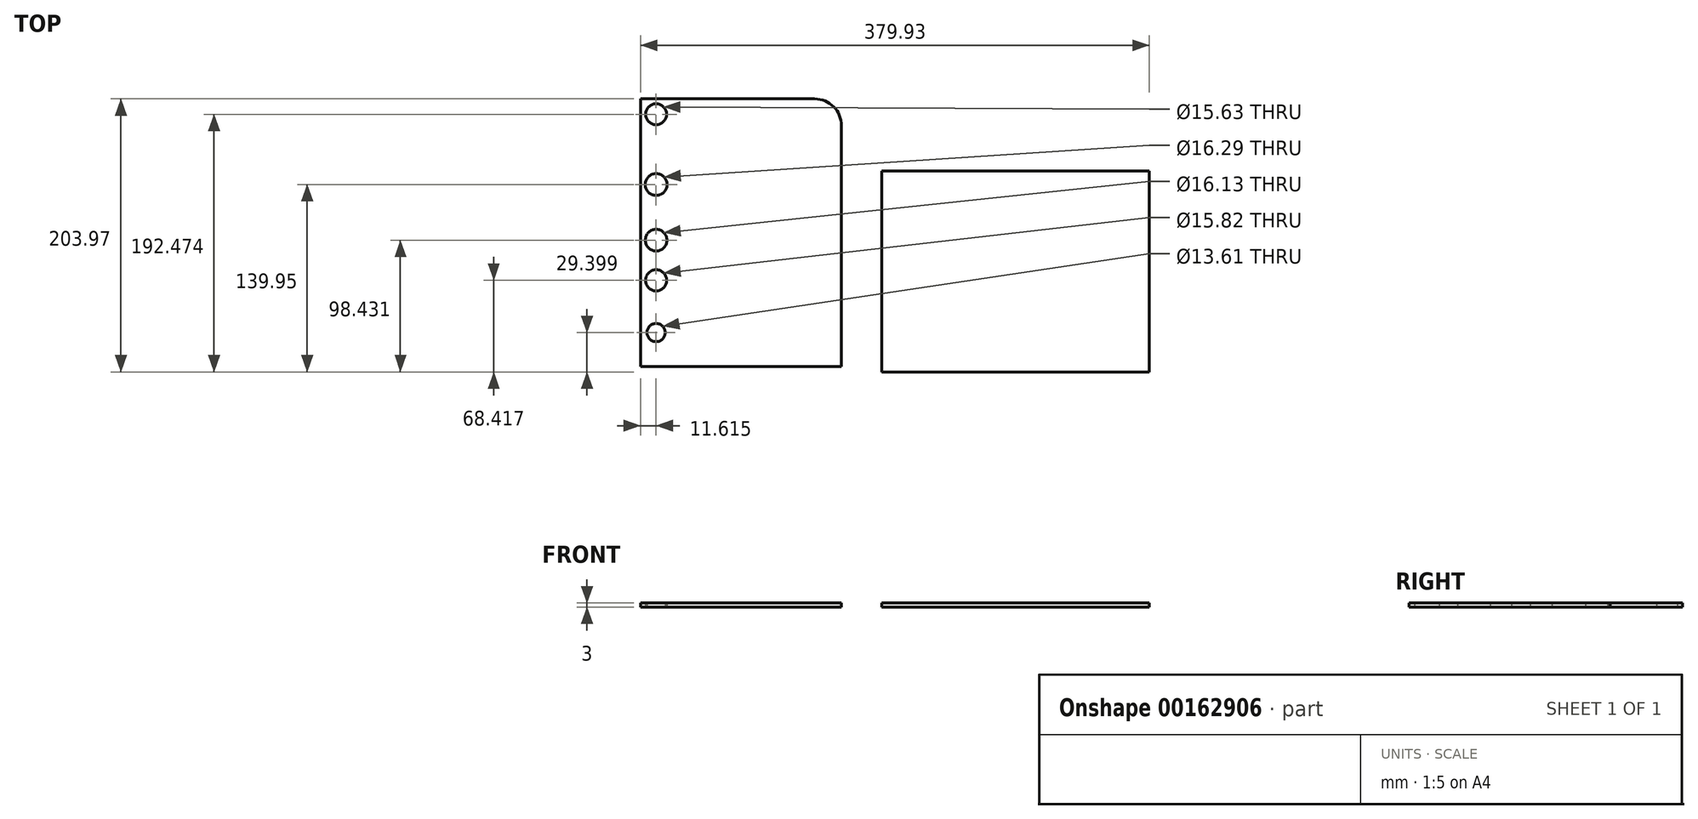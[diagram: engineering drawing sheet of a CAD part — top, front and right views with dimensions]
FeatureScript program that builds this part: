
annotation { "Feature Type Name" : "Feature", "Feature Type Description" : "" }
export const myFeature = defineFeature(function(context is Context, id is Id, definition is map)
    precondition{}
    {
        {
            var Q0;
            Q0=qCreatedBy(makeId("Top.planeOp"),FACE);
            var sketch = newSketch(context, id + "F0", { "sketchPlane" : qUnion([Q0])});
            skLineSegment(sketch, "E0.bottom", {"start": v(-110.78, 14.62) * mm, "end": v(89.22, 14.62) * mm});
            skLineSegment(sketch, "E0.top", {"start": v(-110.78, -135.38) * mm, "end": v(89.22, -135.38) * mm});
            skLineSegment(sketch, "E0.left", {"start": v(-110.78, 14.62) * mm, "end": v(-110.78, -135.38) * mm});
            skLineSegment(sketch, "E0.right", {"start": v(89.22, 14.62) * mm, "end": v(89.22, -135.38) * mm});
            skLineSegment(sketch, "E1.bottom", {"start": v(-290.71, 68.6) * mm, "end": v(-160.71, 68.6) * mm});
            skLineSegment(sketch, "E1.top", {"start": v(-290.71, -131.4) * mm, "end": v(-140.71, -131.4) * mm});
            skLineSegment(sketch, "E1.left", {"start": v(-290.71, 68.6) * mm, "end": v(-290.71, -131.4) * mm});
            skLineSegment(sketch, "E1.right", {"start": v(-140.71, 48.6) * mm, "end": v(-140.71, -131.4) * mm});
            skPoint(sketch, "E2.visualSharp", {"position": v(-140.71, 68.6) * mm});
            skArc(sketch, "E2.filletArc", {"start": v(-140.71, 48.6) * mm, "mid": v(-146.57, 62.73) * mm, "end": v(-160.71, 68.6) * mm});
            skCircle(sketch, "E3", {"center": v(-279.1, 57.1) * mm, "radius": 7.81 * mm});
            skCircle(sketch, "E4", {"center": v(-279.1, 4.57) * mm, "radius": 8.14 * mm});
            skCircle(sketch, "E5", {"center": v(-279.1, -36.95) * mm, "radius": 8.07 * mm});
            skCircle(sketch, "E6", {"center": v(-279.1, -66.96) * mm, "radius": 7.9 * mm});
            skCircle(sketch, "E7", {"center": v(-279.1, -105.98) * mm, "radius": 6.8 * mm});
            skSolve(sketch);
        }
        {
            var Q0;
            Q0 = qSketchRegion(id + "F0", true);
            var Q1;
            Q1=makeQuery(id+"F0.imprint","IMPRINT",FACE,{"disambiguationData":[TD([[makeQuery(id+"F0.imprint","IMPRINT",EDGE,{"derivedFrom":sQuery(id+"F0.wireOp",EDGE,"E0.bottom")}),-1.0]])]});
            extrude(context, id + "F1", {"entities" : qUnion([Q0, Q1]), "depth" : 3 * mm});
        }
    });
